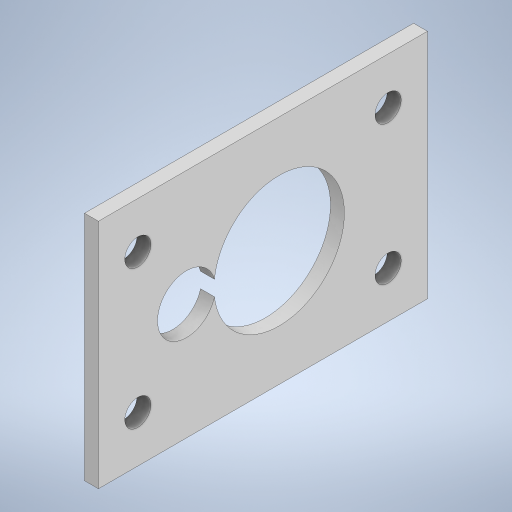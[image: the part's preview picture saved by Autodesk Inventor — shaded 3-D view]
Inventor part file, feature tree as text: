
AUTODESK INVENTOR PART (.ipt)
format: ipt  version: 2023 (Build 270158000, 158)  size: 241,152 bytes
history: native  units: in
note: dims shown in document units (in); Inventor stores cm internally (conversion verified against a paired STEP export)
features: extrude x1, sketch x1
ambient origin geometry x8: Origin, YZ Plane, XZ Plane, XY Plane, X Axis, Y Axis, Z Axis, Center Point
bodies: Solid1 (feature_tree)
feature tree (2):
  extrude  "Extrusion1"  Depth=0.71in
  sketch  "Sketch1"  dims[d0=0.5in d1=0.71in d2=0.75in d3=0.125in d5=0.0563in d9=0.54in d10=0.3in d11=0.3in d12=0.54in d13=0.1in d18=0.03in d19=0.0in d20=0.2812in d21=0.125in d23=0.085in d24=0.085in]
